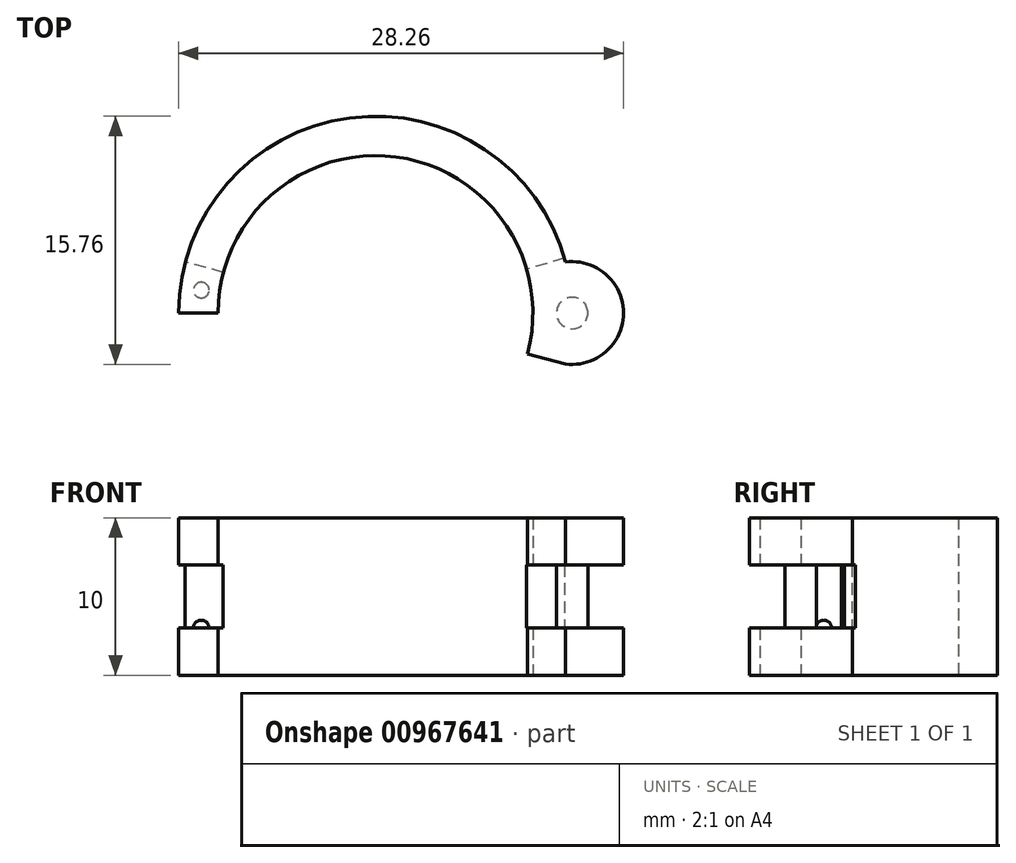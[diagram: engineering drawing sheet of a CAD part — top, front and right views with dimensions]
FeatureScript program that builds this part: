
annotation { "Feature Type Name" : "Feature", "Feature Type Description" : "" }
export const myFeature = defineFeature(function(context is Context, id is Id, definition is map)
    precondition{}
    {
        {
            var Q0;
            Q0=qCreatedBy(makeId("Top.planeOp"),FACE);
            var sketch = newSketch(context, id + "F0", { "sketchPlane" : qUnion([Q0])});
            skArc(sketch, "E0", {"start": v(12.07, -3.24) * mm, "mid": v(1.63, 12.4) * mm, "end": v(-12.5, 0) * mm});
            skLineSegment(sketch, "E1", {"start": v(-12.5, 0) * mm, "end": v(12.5, 0) * mm, "construction": true});
            skCircle(sketch, "E2", {"center": v(0, 0) * mm, "radius": 10 * mm, "construction": true});
            skLineSegment(sketch, "E3", {"start": v(0, 0) * mm, "end": v(12.07, -3.24) * mm, "construction": true});
            skLineSegment(sketch, "E4", {"start": v(0, 0) * mm, "end": v(12.07, 3.24) * mm, "construction": true});
            skArc(sketch, "E5", {"start": v(12.07, -3.24) * mm, "mid": v(15.76, 0) * mm, "end": v(12.07, 3.24) * mm});
            skArc(sketch, "E6", {"start": v(9.66, -2.59) * mm, "mid": v(1.3, 9.91) * mm, "end": v(-10, 0) * mm});
            skLineSegment(sketch, "E7", {"start": v(-12.5, 0) * mm, "end": v(-10, 0) * mm});
            skLineSegment(sketch, "E8", {"start": v(9.66, -2.59) * mm, "end": v(12.07, -3.24) * mm});
            skSolve(sketch);
        }
        {
            var Q0;
            Q0 = qSketchRegion(id + "F0", true);
            extrude(context, id + "F1", {"entities" : qUnion([Q0]), "depth" : 3 * mm, "offsetDistance" : 25 * mm});
        }
        {
            var Q0;
            Q0=makeQuery(id+"F1.opExtrude","CAP_FACE",FACE,{"disambiguationData":[OSD([sQuery(id+"F0.wireOp",EDGE,"E0"),sQuery(id+"F0.wireOp",EDGE,"E5"),sQuery(id+"F0.wireOp",EDGE,"E6"),sQuery(id+"F0.wireOp",EDGE,"E7"),sQuery(id+"F0.wireOp",EDGE,"E8")])],"isStart":false});
            var sketch = newSketch(context, id + "F2", { "sketchPlane" : qUnion([Q0])});
            skCircle(sketch, "E9", {"center": v(12.5, 0) * mm, "radius": 1 * mm});
            skArc(sketch, "E10", {"start": v(12.07, 3.24) * mm, "mid": v(10.8, 2.79) * mm, "end": v(9.82, 1.87) * mm, "construction": true});
            skPoint(sketch, "E11", {"position": v(9.82, 1.87) * mm});
            skPoint(sketch, "E12", {"position": v(12.07, 3.24) * mm});
            skLineSegment(sketch, "E13", {"start": v(0, 0) * mm, "end": v(-12.07, 3.24) * mm, "construction": true});
            skLineSegment(sketch, "E14", {"start": v(-12.5, 0) * mm, "end": v(12.5, 0) * mm, "construction": true});
            skLineSegment(sketch, "E15", {"start": v(-9.66, 2.59) * mm, "end": v(-12.07, 3.24) * mm});
            skArc(sketch, "E16.0", {"start": v(12, 3.48) * mm, "mid": v(10.76, 3.05) * mm, "end": v(9.76, 2.2) * mm, "construction": true});
            skLineSegment(sketch, "E17", {"start": v(12, 3.48) * mm, "end": v(9.6, 2.78) * mm});
            skSolve(sketch);
        }
        {
            var Q0;
            Q0=makeQuery(id+"F2.imprint","IMPRINT",FACE,{"disambiguationData":[TD([[makeQuery(id+"F2.imprint","IMPRINT",EDGE,{"derivedFrom":sQuery(id+"F2.wireOp",EDGE,"E9")}),1.0]])]});
            var Q1;
            {var subQ0=sQuery(id+"F2.wireOp",EDGE,"E15");Q1=makeQuery(id+"F2.imprint","IMPRINT",FACE,{"disambiguationData":[TD([[makeQuery(id+"F2.imprint","IMPRINT",EDGE,{"derivedFrom":subQ0}),-1.0]])]});}
            var Q2;
            Q2=sQuery(id+"F2.wireOp",EDGE,"E9");
            extrude(context, id + "F3", {"entities" : qUnion([Q0, Q1]), "operationType" : NewBodyOperationType.ADD, "surfaceOperationType" : NewSurfaceOperationType.ADD, "surfaceEntities" : qUnion([Q2]), "depth" : 4 * mm, "offsetDistance" : 25 * mm});
        }
        {
            var Q0;
            Q0=makeQuery(id+"F3.opExtrude","CAP_FACE",FACE,{"disambiguationData":[OSD([sQuery(id+"F2.wireOp",EDGE,"E9")])],"isStart":false});
            var sketch = newSketch(context, id + "F4", { "sketchPlane" : qUnion([Q0])});
            skArc(sketch, "E18", {"start": v(12.07, -3.24) * mm, "mid": v(1.63, 12.4) * mm, "end": v(-12.5, 0) * mm});
            skLineSegment(sketch, "E19", {"start": v(-12.5, 0) * mm, "end": v(12.5, 0) * mm, "construction": true});
            skCircle(sketch, "E20", {"center": v(0, 0) * mm, "radius": 10 * mm, "construction": true});
            skLineSegment(sketch, "E21", {"start": v(0, 0) * mm, "end": v(12.07, -3.24) * mm, "construction": true});
            skLineSegment(sketch, "E22", {"start": v(0, 0) * mm, "end": v(12.07, 3.24) * mm, "construction": true});
            skArc(sketch, "E23", {"start": v(12.07, -3.24) * mm, "mid": v(15.76, 0) * mm, "end": v(12.07, 3.24) * mm});
            skArc(sketch, "E24", {"start": v(9.66, -2.59) * mm, "mid": v(1.3, 9.91) * mm, "end": v(-10, 0) * mm});
            skLineSegment(sketch, "E25", {"start": v(-12.5, 0) * mm, "end": v(-10, 0) * mm});
            skLineSegment(sketch, "E26", {"start": v(9.66, -2.59) * mm, "end": v(12.07, -3.24) * mm});
            skSolve(sketch);
        }
        {
            var Q0;
            Q0 = qSketchRegion(id + "F4", true);
            extrude(context, id + "F5", {"entities" : qUnion([Q0]), "operationType" : NewBodyOperationType.ADD, "depth" : 3 * mm, "offsetDistance" : 25 * mm});
        }
        {
            var Q0;
            {var subQ0=sQuery(id+"F0.wireOp",EDGE,"E6");var subQ1=sQuery(id+"F0.wireOp",EDGE,"E7");var subQ2=sQuery(id+"F0.wireOp",EDGE,"E0");Q0=makeQuery(id+"F3.boolean.opBoolean","SPLIT",FACE,{"disambiguationData":[TD([makeQuery(id+"F1.opExtrude","SWEPT_FACE",FACE,{"disambiguationData":[OSD([subQ1])]})])],"derivedFrom":makeQuery(id+"F1.opExtrude","CAP_FACE",FACE,{"disambiguationData":[OSD([subQ2,sQuery(id+"F0.wireOp",EDGE,"E5"),subQ0,subQ1,sQuery(id+"F0.wireOp",EDGE,"E8")])],"isStart":false})});}
            var sketch = newSketch(context, id + "F6", { "sketchPlane" : qUnion([Q0])});
            skArc(sketch, "E27", {"start": v(-11, 1.95) * mm, "mid": v(-11.55, 1.52) * mm, "end": v(-11.12, 0.96) * mm});
            skLineSegment(sketch, "E28", {"start": v(-10.87, 2.91) * mm, "end": v(-11.25, 0) * mm, "construction": true});
            skLineSegment(sketch, "E29", {"start": v(-9.91, 1.3) * mm, "end": v(-12.4, 1.63) * mm, "construction": true});
            skLineSegment(sketch, "E30", {"start": v(-11, 1.95) * mm, "end": v(-11.12, 0.96) * mm});
            skSolve(sketch);
        }
        {
            var Q0;
            Q0 = qSketchRegion(id + "F6", true);
            var Q1;
            Q1=sQuery(id+"F6.wireOp",EDGE,"E28");
            revolve(context, id + "F7", {"operationType" : NewBodyOperationType.ADD, "surfaceOperationType" : NewSurfaceOperationType.NEW, "entities" : qUnion([Q0]), "axis" : qUnion([Q1]), "revolveType" : RevolveType.FULL});
        }
    });
